# Revit family: Side Wall Grille-Small-Rectangular Connection-Return & Extact
name_source: partatom
category: Air Terminals
revit_build: Autodesk Revit MEP 2013 (Build: 20130531_2115(x64)
units: mm (PartAtom-declared; Revit-internal decimal feet)

## types (12) — shared parameters
Diffuser Service = SG
Flange Thk = 20 mm
Flange Width = 25 mm
zero-valued in all types: Neck Size

## per-type parameters (varying)
| type | Air Terminal Type | Colour | Damper Material | Grille Height | Grilles Tag | Manufacturer | Material | Model | No.of Fins |
| Side Wall Grille-Supply-Small-150mm | DOUBLE DEFLECTION GRILLE (SUPPLY) | BY ARCHITECT | S.S. | 300 mm |  | EH PRICE | POWDER COATED AC | 7200 | 11 |
| Side Wall Grille-Supply-Small-100mm |  |  |  | 100 mm |  |  |  |  | 3 |
| Side Wall Grille-Supply-Small-200mm | DOUBLE DEFLECTION GRILLE (SUPPLY) | BY ARCHITECT | S.S. | 200 mm | SG-3 | EH PRICE | POWDER COATED AC | 7200 | 7 |
| Side Wall Grille-Supply-Small-250mm |  |  |  | 250 mm |  |  |  |  | 9 |
| Side Wall Grille-Supply-Small-300mm | DOUBLE DEFLECTION GRILLE (SUPPLY) | BY ARCHITECT | S.S. | 250 mm |  | EH PRICE | POWDER COATED AC | 7200 | 9 |
| Side Wall Grille-Supply-Small-350 | DOUBLE DEFLECTION GRILLE (SUPPLY) | BY ARCHITECT | S.S. | 350 mm |  | EH PRICE | POWDER COATED AC | 7200 | 13 |
| Side Wall Grille-Return-Small-300mm |  |  |  | 300 mm |  |  |  |  | 11 |
| Side Wall Grille-Return-Small-250mm |  |  |  | 250 mm |  |  |  |  | 9 |
| Side Wall Grille-Return-Small-200mm | DOUBLE DEFLECTION GRILLE (SUPPLY) | BY ARCHITECT | S.S. | 200 mm | SG-3 | EH PRICE | POWDER COATED AC | 7200 | 7 |
| Side Wall Grille-Return-Small-100mm |  |  |  | 100 mm |  |  |  |  | 3 |
| Side Wall Grille-Return-Small-150mm |  |  |  | 150 mm |  |  |  |  | 5 |
| Side Wall Grille-Supply-Small | DOUBLE DEFLECTION GRILLE (SUPPLY) | BY ARCHITECT | S.S. | 150 mm | SG-2 | EH PRICE | POWDER COATED AC | 7200 | 5 |

## geometry (parser evidence)
native form markers: Blend x8, Sweep x5
no freeform markers — native parametric forms only
